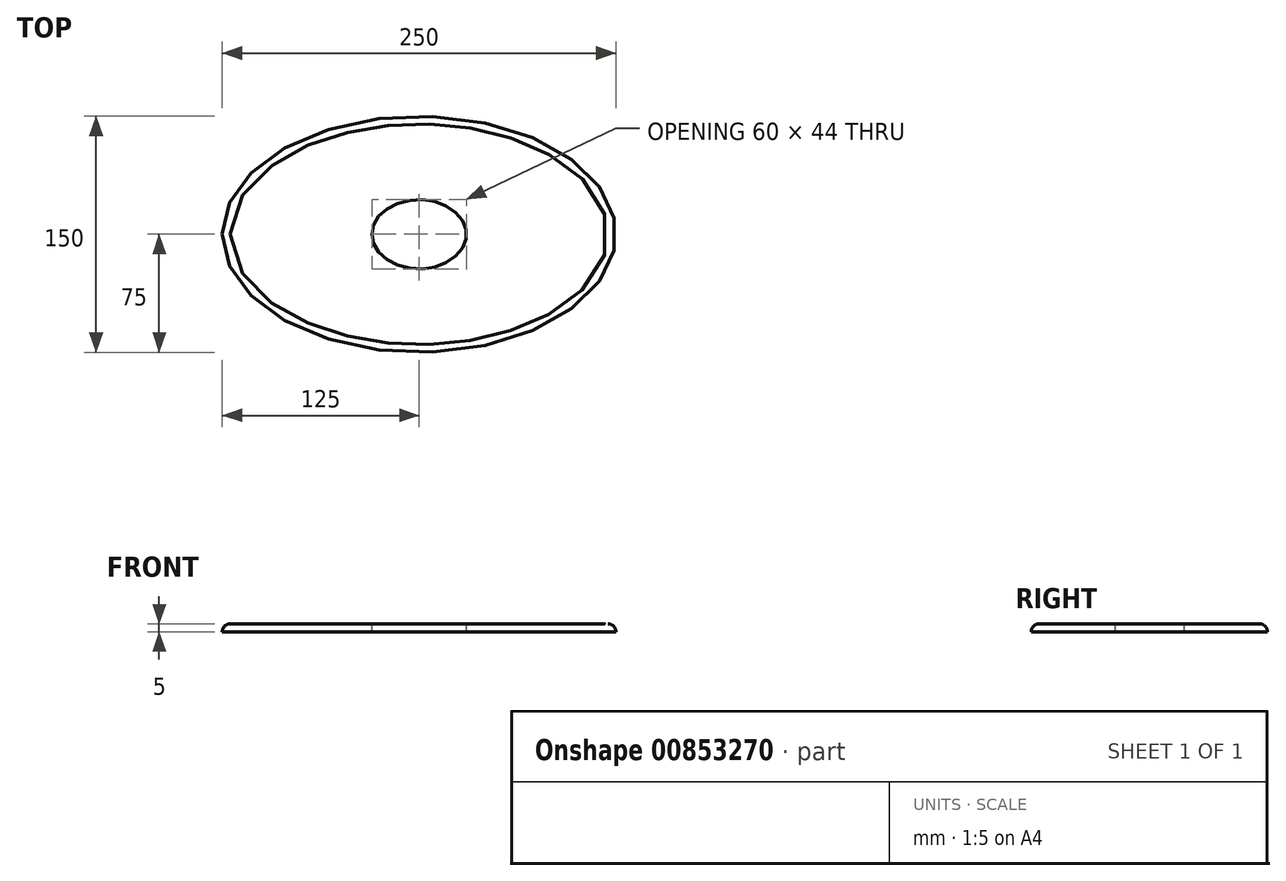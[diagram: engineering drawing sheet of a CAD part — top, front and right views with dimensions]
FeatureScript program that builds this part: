
annotation { "Feature Type Name" : "Feature", "Feature Type Description" : "" }
export const myFeature = defineFeature(function(context is Context, id is Id, definition is map)
    precondition{}
    {
        {
            var Q0;
            Q0=qCreatedBy(makeId("Top.planeOp"),FACE);
            var sketch = newSketch(context, id + "F0", { "sketchPlane" : qUnion([Q0])});
            skEllipse(sketch, "E0", {"center": v(0, 0) * mm, "majorRadius": 125 * mm, "minorRadius": 75 * mm, "majorAxis": v(-1, 0)});
            skSolve(sketch);
        }
        {
            var Q0;
            Q0 = qSketchRegion(id + "F0", true);
            extrude(context, id + "F1", {"entities" : qUnion([Q0]), "depth" : 5 * mm, "offsetDistance" : 25 * mm});
        }
        {
            var Q0;
            Q0=makeQuery(id+"F1.opExtrude","CAP_FACE",FACE,{"disambiguationData":[OSD([sQuery(id+"F0.wireOp",EDGE,"E0")])],"isStart":false});
            fillet(context, id + "F2", {"entities" : qUnion([Q0]), "radius" : 5 * mm, "tangentPropagation" : true, "allowEdgeOverflow" : false});
        }
        {
            var Q0;
            Q0=makeQuery(id+"F1.opExtrude","CAP_FACE",FACE,{"disambiguationData":[OSD([sQuery(id+"F0.wireOp",EDGE,"E0")])],"isStart":false});
            var sketch = newSketch(context, id + "F3", { "sketchPlane" : qUnion([Q0])});
            skEllipse(sketch, "E1", {"center": v(0, 0) * mm, "majorRadius": 30 * mm, "minorRadius": 22 * mm, "majorAxis": v(-1, 0)});
            skSolve(sketch);
        }
        {
            var Q0;
            Q0 = qSketchRegion(id + "F3", true);
            extrude(context, id + "F4", {"entities" : qUnion([Q0]), "operationType" : NewBodyOperationType.REMOVE, "oppositeDirection" : true, "depth" : 25 * mm, "offsetDistance" : 25 * mm});
        }
    });
